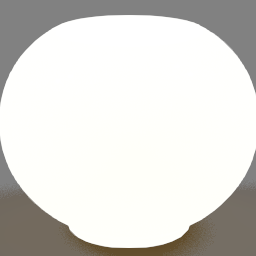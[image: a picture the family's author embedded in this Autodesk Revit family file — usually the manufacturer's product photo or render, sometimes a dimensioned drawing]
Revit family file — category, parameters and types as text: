
# Revit family: 3-110X-xx Galaxy Mirror
name_source: partatom
category: Luminarias
units: mm (PartAtom-declared; Revit-internal decimal feet)

## family parameters
Anfitrión = Muro
Compartido = No
Corte con vacíos al cargar = No
Cota de conector redondo = Diámetro de uso
Número OmniClass = 23.80.70.00
Origen de luz = No
Punto de cálculo de habitación = No
Siempre vertical = Sí
Tipo de pieza = Normal
Título OmniClass = Lighting

## types (4) — shared parameters
Diffuser = Ghost Mirror
Fabricante = Vanita by Oxygen
Lámpara = LED Array
Metal Finish 1 = 15 - Black
Modelo = 3-110X-xx / Galaxy
References = Ref. 3 = 120 V / Ref. 37 = 277 V
URL = www.oxygenlighting.com
Voltage = 120 V
Voltage Input = 120 V or 277 V - 50/60 Hz
zero-valued in all types: Elevación por defecto

## per-type parameters (varying)
| type | Comentarios de vataje | Height | Width |
| 3-1101-15 / Black | 1 x 62.4 W at 120 V | 914 mm  [stored 2.99869 ft] | 610 mm  [stored 2.00131 ft] |
| 3-1103-15 / Black | 1 x 85 W at 120 V | 914 mm  [stored 2.99869 ft] | 1219 mm |
| 3-1104-15 / Black | 1 x 127.8 W at 120 V | 1067 mm  [stored 3.50066 ft] | 1524 mm  [stored 5 ft] |
| 3-1102-15 / Black | 1 x 68.4 W at 120 V | 914 mm  [stored 2.99869 ft] | 914 mm  [stored 2.99869 ft] |

note: [stored X ft] marks values corroborated as IEEE doubles in the binary element streams (Revit-internal decimal feet)

## geometry (parser evidence)
native form markers: Sweep x5
no freeform markers — native parametric forms only
